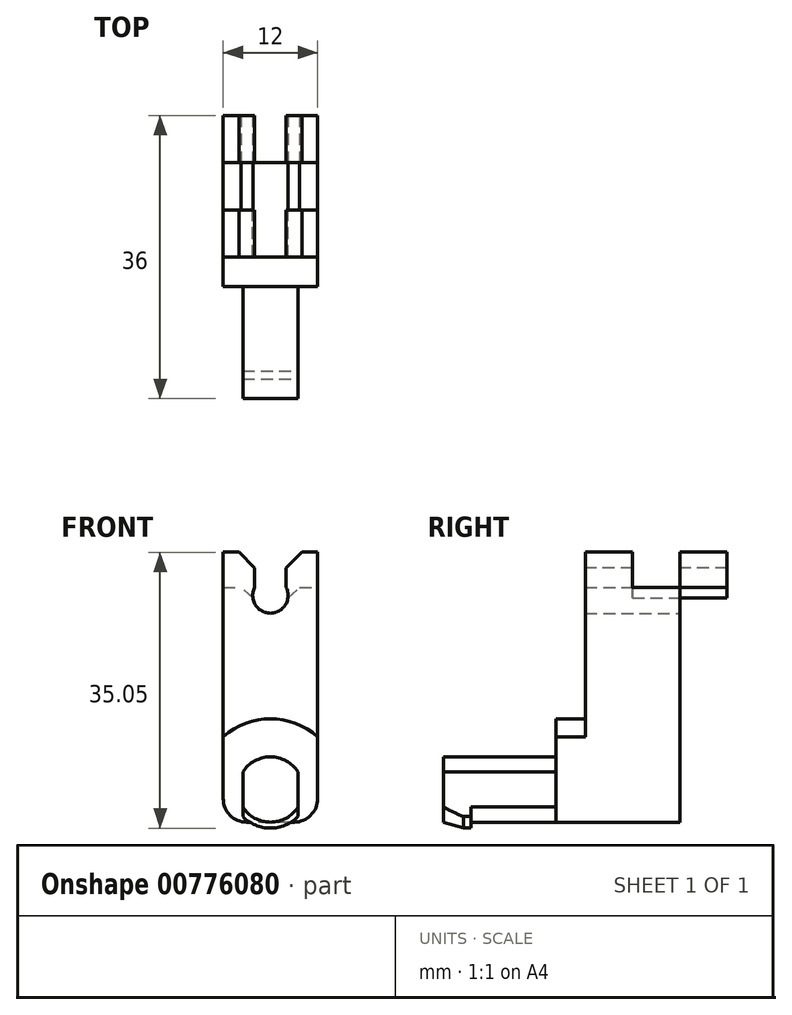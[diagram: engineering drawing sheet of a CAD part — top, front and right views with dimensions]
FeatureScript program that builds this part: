
annotation { "Feature Type Name" : "Feature", "Feature Type Description" : "" }
export const myFeature = defineFeature(function(context is Context, id is Id, definition is map)
    precondition{}
    {
        {
            var Q0;
            Q0=qCreatedBy(makeId("Right.planeOp"),FACE);
            var sketch = newSketch(context, id + "F0", { "sketchPlane" : qUnion([Q0])});
            skLineSegment(sketch, "E0.bottom", {"start": v(-25.14, 2.61) * mm, "end": v(-19.14, 2.61) * mm});
            skLineSegment(sketch, "E0.top", {"start": v(-25.14, -15.39) * mm, "end": v(-19.14, -15.39) * mm});
            skLineSegment(sketch, "E0.left", {"start": v(-25.14, 2.61) * mm, "end": v(-25.14, -15.39) * mm});
            skLineSegment(sketch, "E0.right", {"start": v(-19.14, 2.61) * mm, "end": v(-19.14, -15.39) * mm});
            skSolve(sketch);
        }
        {
            var Q0;
            Q0=makeQuery(id+"F0.imprint","IMPRINT",FACE,{"disambiguationData":[TD([[makeQuery(id+"F0.imprint","IMPRINT",EDGE,{"derivedFrom":sQuery(id+"F0.wireOp",EDGE,"E0.bottom")}),-1.0]])]});
            extrude(context, id + "F1", {"entities" : qUnion([Q0]), "depth" : 8 * mm, "offsetDistance" : 25 * mm});
        }
        {
            var Q0;
            Q0=makeQuery(id+"F1.opExtrude","SWEPT_FACE",FACE,{"disambiguationData":[OSD([sQuery(id+"F0.wireOp",EDGE,"E0.left")])]});
            var sketch = newSketch(context, id + "F2", { "sketchPlane" : qUnion([Q0])});
            skCircle(sketch, "E1", {"center": v(4, -19.54) * mm, "radius": 4.15 * mm});
            skSolve(sketch);
        }
        {
            var Q0;
            Q0=makeQuery(id+"F2.imprint","IMPRINT",FACE,{"disambiguationData":[TD([[makeQuery(id+"F2.imprint","IMPRINT",EDGE,{"derivedFrom":sQuery(id+"F2.wireOp",EDGE,"E1")}),1.0]])]});
            extrude(context, id + "F3", {"entities" : qUnion([Q0]), "depth" : 18 * mm, "offsetDistance" : 25 * mm});
        }
        {
            var Q0;
            Q0=makeQuery(id+"F3.opExtrude","CAP_FACE",FACE,{"disambiguationData":[OSD([sQuery(id+"F2.wireOp",EDGE,"E1")])],"isStart":true});
            var Q1;
            Q1=makeQuery(id+"F1.opExtrude","SWEPT_FACE",FACE,{"disambiguationData":[OSD([sQuery(id+"F0.wireOp",EDGE,"E0.right")])]});
            extrude(context, id + "F4", {"entities" : qUnion([Q0]), "endBound" : BoundingType.UP_TO_SURFACE, "depth" : 25 * mm, "endBoundEntityFace" : qUnion([Q1]), "offsetDistance" : 25 * mm});
        }
        {
            var Q0;
            Q0=makeQuery(id+"F1.opExtrude","SWEPT_FACE",FACE,{"disambiguationData":[OSD([sQuery(id+"F0.wireOp",EDGE,"E0.top")])]});
            var Q1;
            Q1=makeQuery(id+"F4.opExtrude","SWEPT_FACE",FACE,{"disambiguationData":[OSD([sQuery(id+"F2.wireOp",EDGE,"E1")])]});
            extrude(context, id + "F5", {"entities" : qUnion([Q0]), "depth" : (8.4 / 2) * mm, "endBoundEntityFace" : qUnion([Q1]), "offsetDistance" : 25 * mm});
        }
        {
            var Q0;
            Q0=makeQuery(id+"F3.opExtrude","SWEPT_BODY",BODY,{"disambiguationData":[OSD([sQuery(id+"F2.wireOp",EDGE,"E1")])]});
            var Q1;
            Q1=makeQuery(id+"F4.opExtrude","SWEPT_BODY",BODY,{"disambiguationData":[OSD([sQuery(id+"F2.wireOp",EDGE,"E1")])]});
            var Q2;
            Q2=makeQuery(id+"F5.opExtrude","SWEPT_BODY",BODY,{"disambiguationData":[OSD([sQuery(id+"F0.wireOp",EDGE,"E0.top")])]});
            var Q3;
            Q3=makeQuery(id+"F1.opExtrude","SWEPT_BODY",BODY,{"disambiguationData":[OSD([sQuery(id+"F0.wireOp",EDGE,"E0.bottom"),sQuery(id+"F0.wireOp",EDGE,"E0.top"),sQuery(id+"F0.wireOp",EDGE,"E0.left"),sQuery(id+"F0.wireOp",EDGE,"E0.right")])]});
            booleanBodies(context, id + "F6", {"operationType" : BooleanOperationType.UNION, "tools" : qUnion([Q0, Q1, Q2, Q3])});
        }
        {
            var Q0;
            {var subQ0=sQuery(id+"F0.wireOp",EDGE,"E0.top");Q0=makeQuery(id+"F6.opBoolean","MERGE",FACE,{"derivedFrom":[makeQuery(id+"F1.opExtrude","CAP_FACE",FACE,{"disambiguationData":[OSD([sQuery(id+"F0.wireOp",EDGE,"E0.bottom"),subQ0,sQuery(id+"F0.wireOp",EDGE,"E0.left"),sQuery(id+"F0.wireOp",EDGE,"E0.right")])],"isStart":false}),makeQuery(id+"F5.opExtrude","SWEPT_FACE",FACE,{"disambiguationData":[OSD([subQ0]),TDD([makeQuery(id+"F1.opExtrude","CAP_EDGE",EDGE,{"disambiguationData":[OSD([subQ0])],"isStart":false})])]})]});}
            var Q1;
            {var subQ0=sQuery(id+"F0.wireOp",EDGE,"E0.top");Q1=makeQuery(id+"F6.opBoolean","MERGE",FACE,{"derivedFrom":[makeQuery(id+"F1.opExtrude","CAP_FACE",FACE,{"disambiguationData":[OSD([sQuery(id+"F0.wireOp",EDGE,"E0.bottom"),subQ0,sQuery(id+"F0.wireOp",EDGE,"E0.left"),sQuery(id+"F0.wireOp",EDGE,"E0.right")])],"isStart":true}),makeQuery(id+"F5.opExtrude","SWEPT_FACE",FACE,{"disambiguationData":[OSD([subQ0]),TDD([makeQuery(id+"F1.opExtrude","CAP_EDGE",EDGE,{"disambiguationData":[OSD([subQ0])],"isStart":true})])]})]});}
            cPlane(context, id + "F7", {"entities" : qUnion([Q0, Q1]), "cplaneType" : CPlaneType.MID_PLANE, "offset" : 25 * mm, "width" : 150 * mm, "height" : 150 * mm});
        }
        {
            var Q0;
            Q0=qCreatedBy(id+"F7.planeOp",FACE);
            var sketch = newSketch(context, id + "F8", { "sketchPlane" : qUnion([Q0])});
            skLineSegment(sketch, "E2", {"start": v(-39.64, -15.39) * mm, "end": v(-39.64, -14.64) * mm});
            skLineSegment(sketch, "E3", {"start": v(-39.64, -14.64) * mm, "end": v(-40.64, -14.64) * mm});
            skLineSegment(sketch, "E4", {"start": v(-40.64, -14.64) * mm, "end": v(-43.14, -15.39) * mm});
            skLineSegment(sketch, "E5", {"start": v(-43.14, -15.39) * mm, "end": v(-39.64, -15.39) * mm});
            skSolve(sketch);
        }
        {
            var Q0;
            Q0=makeQuery(id+"F8.imprint","IMPRINT",FACE,{"disambiguationData":[TD([[makeQuery(id+"F8.imprint","IMPRINT",EDGE,{"derivedFrom":sQuery(id+"F8.wireOp",EDGE,"E2")}),1.0]])]});
            var Q1;
            {var subQ0=sQuery(id+"F2.wireOp",EDGE,"E1");Q1=makeQuery(id+"F6.opBoolean","MERGE",FACE,{"derivedFrom":[makeQuery(id+"F3.opExtrude","SWEPT_FACE",FACE,{"disambiguationData":[OSD([subQ0])]}),makeQuery(id+"F4.opExtrude","SWEPT_FACE",FACE,{"disambiguationData":[OSD([subQ0])]})]});}
            revolve(context, id + "F9", {"operationType" : NewBodyOperationType.ADD, "surfaceOperationType" : NewSurfaceOperationType.NEW, "entities" : qUnion([Q0]), "axis" : qUnion([Q1]), "revolveType" : RevolveType.SYMMETRIC, "angle" : 360 * degree});
        }
        {
            var Q0;
            Q0=makeQuery(id+"F1.opExtrude","SWEPT_FACE",FACE,{"disambiguationData":[OSD([sQuery(id+"F0.wireOp",EDGE,"E0.bottom")])]});
            extrude(context, id + "F10", {"entities" : qUnion([Q0]), "depth" : 6 * mm, "offsetDistance" : 25 * mm});
        }
        {
            var Q0;
            Q0=makeQuery(id+"F10.opExtrude","SWEPT_FACE",FACE,{"disambiguationData":[OSD([sQuery(id+"F0.wireOp",EDGE,"E0.bottom"),sQuery(id+"F0.wireOp",EDGE,"E0.right")])]});
            var sketch = newSketch(context, id + "F11", { "sketchPlane" : qUnion([Q0])});
            skCircle(sketch, "E6", {"center": v(-4, 5.11) * mm, "radius": 2.25 * mm});
            skSolve(sketch);
        }
        {
            var Q0;
            Q0=makeQuery(id+"F10.opExtrude","SWEPT_BODY",BODY,{"disambiguationData":[OSD([sQuery(id+"F0.wireOp",EDGE,"E0.bottom")])]});
            var Q1;
            Q1=makeQuery(id+"F3.opExtrude","SWEPT_BODY",BODY,{"disambiguationData":[OSD([sQuery(id+"F2.wireOp",EDGE,"E1")])]});
            booleanBodies(context, id + "F12", {"operationType" : BooleanOperationType.UNION, "tools" : qUnion([Q0, Q1])});
        }
        {
            var Q0;
            Q0=makeQuery(id+"F11.imprint","IMPRINT",FACE,{"disambiguationData":[TD([[makeQuery(id+"F11.imprint","IMPRINT",EDGE,{"derivedFrom":sQuery(id+"F11.wireOp",EDGE,"E6")}),1.0]])]});
            extrude(context, id + "F13", {"entities" : qUnion([Q0]), "operationType" : NewBodyOperationType.REMOVE, "oppositeDirection" : true, "depth" : 25 * mm, "offsetDistance" : 25 * mm});
        }
        {
            var Q0;
            {var subQ4=sQuery(id+"F11.wireOp",EDGE,"E6");Q0=makeQuery(id+"F11.imprint","IMPRINT",FACE,{"disambiguationData":[TD([[makeQuery(id+"F11.imprint","IMPRINT",EDGE,{"derivedFrom":subQ4}),-1.0]])]});}
            var sketch = newSketch(context, id + "F14", { "sketchPlane" : qUnion([Q0])});
            skLineSegment(sketch, "E7.bottom", {"start": v(-6, 9.61) * mm, "end": v(-2, 9.61) * mm});
            skLineSegment(sketch, "E7.top", {"start": v(-6, 5.11) * mm, "end": v(-2, 5.11) * mm});
            skLineSegment(sketch, "E7.left", {"start": v(-6, 9.61) * mm, "end": v(-6, 5.11) * mm});
            skLineSegment(sketch, "E7.right", {"start": v(-2, 9.61) * mm, "end": v(-2, 5.11) * mm});
            skSolve(sketch);
        }
        {
            var Q0;
            Q0 = qSketchRegion(id + "F14", true);
            extrude(context, id + "F15", {"entities" : qUnion([Q0]), "operationType" : NewBodyOperationType.REMOVE, "oppositeDirection" : true, "depth" : 25 * mm, "offsetDistance" : 25 * mm});
        }
        {
            var Q0;
            {var subQ0=sQuery(id+"F0.wireOp",EDGE,"E0.left");Q0=makeQuery(id+"F12.opBoolean","MERGE",FACE,{"derivedFrom":[makeQuery(id+"F6.opBoolean","MERGE",FACE,{"derivedFrom":[makeQuery(id+"F1.opExtrude","SWEPT_FACE",FACE,{"disambiguationData":[OSD([subQ0])]}),makeQuery(id+"F4.opExtrude","CAP_FACE",FACE,{"disambiguationData":[OSD([sQuery(id+"F2.wireOp",EDGE,"E1")])],"isStart":true}),makeQuery(id+"F5.opExtrude","SWEPT_FACE",FACE,{"disambiguationData":[OSD([sQuery(id+"F0.wireOp",EDGE,"E0.top"),subQ0])]})]}),makeQuery(id+"F10.opExtrude","SWEPT_FACE",FACE,{"disambiguationData":[OSD([sQuery(id+"F0.wireOp",EDGE,"E0.bottom"),subQ0])]})]});}
            var sketch = newSketch(context, id + "F16", { "sketchPlane" : qUnion([Q0])});
            skLineSegment(sketch, "E8.bottom", {"start": v(-2, -9.26) * mm, "end": v(0.5, -9.26) * mm});
            skLineSegment(sketch, "E8.top", {"start": v(-2, -26.84) * mm, "end": v(0.5, -26.84) * mm});
            skLineSegment(sketch, "E8.left", {"start": v(-2, -9.26) * mm, "end": v(-2, -26.84) * mm});
            skLineSegment(sketch, "E8.right", {"start": v(0.5, -9.26) * mm, "end": v(0.5, -26.84) * mm});
            skLineSegment(sketch, "E9.bottom", {"start": v(11, -9.26) * mm, "end": v(7.5, -9.26) * mm});
            skLineSegment(sketch, "E9.top", {"start": v(11, -26.84) * mm, "end": v(7.5, -26.84) * mm});
            skLineSegment(sketch, "E9.left", {"start": v(11, -9.26) * mm, "end": v(11, -26.84) * mm});
            skLineSegment(sketch, "E9.right", {"start": v(7.5, -9.26) * mm, "end": v(7.5, -26.84) * mm});
            skSolve(sketch);
        }
        {
            var Q0;
            Q0 = qSketchRegion(id + "F16", true);
            extrude(context, id + "F17", {"entities" : qUnion([Q0]), "operationType" : NewBodyOperationType.REMOVE, "endBound" : BoundingType.THROUGH_ALL, "depth" : 25 * mm, "offsetDistance" : 25 * mm});
        }
        {
            var Q0;
            {var subQ1=sQuery(id+"F0.wireOp",EDGE,"E0.bottom");Q0=makeQuery(id+"F15.boolean.opBoolean","SPLIT",FACE,{"disambiguationData":[TD([makeQuery(id+"F15.opExtrude","SWEPT_FACE",FACE,{"disambiguationData":[OSD([sQuery(id+"F14.wireOp",EDGE,"E7.right")])]})])],"derivedFrom":makeQuery(id+"F10.opExtrude","CAP_FACE",FACE,{"disambiguationData":[OSD([subQ1])],"isStart":false})});}
            var sketch = newSketch(context, id + "F18", { "sketchPlane" : qUnion([Q0])});
            skLineSegment(sketch, "E10.bottom", {"start": v(-2, -19.14) * mm, "end": v(0, -19.14) * mm});
            skLineSegment(sketch, "E10.top", {"start": v(-2, -25.14) * mm, "end": v(0, -25.14) * mm});
            skLineSegment(sketch, "E10.left", {"start": v(-2, -19.14) * mm, "end": v(-2, -25.14) * mm});
            skLineSegment(sketch, "E10.right", {"start": v(0, -19.14) * mm, "end": v(0, -25.14) * mm});
            skPoint(sketch, "E11.oppositeSnap0", {"position": v(0, -22.14) * mm});
            skLineSegment(sketch, "E11.bottom", {"start": v(8, -19.14) * mm, "end": v(10, -19.14) * mm});
            skLineSegment(sketch, "E11.top", {"start": v(8, -25.14) * mm, "end": v(10, -25.14) * mm});
            skLineSegment(sketch, "E11.left", {"start": v(8, -19.14) * mm, "end": v(8, -25.14) * mm});
            skLineSegment(sketch, "E11.right", {"start": v(10, -19.14) * mm, "end": v(10, -25.14) * mm});
            skSolve(sketch);
        }
        {
            var Q0;
            Q0=makeQuery(id+"F18.imprint","IMPRINT",FACE,{"disambiguationData":[TD([[makeQuery(id+"F18.imprint","IMPRINT",EDGE,{"derivedFrom":sQuery(id+"F18.wireOp",EDGE,"E10.bottom")}),-1.0]])]});
            var Q1;
            Q1=makeQuery(id+"F18.imprint","IMPRINT",FACE,{"disambiguationData":[TD([[makeQuery(id+"F18.imprint","IMPRINT",EDGE,{"derivedFrom":sQuery(id+"F18.wireOp",EDGE,"E11.bottom")}),-1.0]])]});
            extrude(context, id + "F19", {"entities" : qUnion([Q0, Q1]), "operationType" : NewBodyOperationType.ADD, "oppositeDirection" : true, "depth" : 30 * mm, "offsetDistance" : 25 * mm});
        }
        {
            var Q0;
            {var subQ0=sQuery(id+"F0.wireOp",EDGE,"E0.right");Q0=makeQuery(id+"F19.boolean.opBoolean","MERGE",FACE,{"derivedFrom":[makeQuery(id+"F12.opBoolean","MERGE",FACE,{"derivedFrom":[makeQuery(id+"F6.opBoolean","MERGE",FACE,{"derivedFrom":[makeQuery(id+"F1.opExtrude","SWEPT_FACE",FACE,{"disambiguationData":[OSD([subQ0])]}),makeQuery(id+"F4.opExtrude","CAP_FACE",FACE,{"disambiguationData":[OSD([sQuery(id+"F2.wireOp",EDGE,"E1")])],"isStart":false}),makeQuery(id+"F5.opExtrude","SWEPT_FACE",FACE,{"disambiguationData":[OSD([sQuery(id+"F0.wireOp",EDGE,"E0.top"),subQ0])]})]}),makeQuery(id+"F10.opExtrude","SWEPT_FACE",FACE,{"disambiguationData":[OSD([sQuery(id+"F0.wireOp",EDGE,"E0.bottom"),subQ0])]})]}),makeQuery(id+"F19.opExtrude","SWEPT_FACE",FACE,{"disambiguationData":[OSD([sQuery(id+"F18.wireOp",EDGE,"E10.bottom")])]}),makeQuery(id+"F19.opExtrude","SWEPT_FACE",FACE,{"disambiguationData":[OSD([sQuery(id+"F18.wireOp",EDGE,"E11.bottom")])]})]});}
            var sketch = newSketch(context, id + "F20", { "sketchPlane" : qUnion([Q0])});
            skLineSegment(sketch, "E12.bottom", {"start": v(-10, -13.69) * mm, "end": v(2, -13.69) * mm});
            skLineSegment(sketch, "E12.top", {"start": v(-10, -23.69) * mm, "end": v(2, -23.69) * mm});
            skLineSegment(sketch, "E12.left", {"start": v(-10, -13.69) * mm, "end": v(-10, -23.69) * mm});
            skLineSegment(sketch, "E12.right", {"start": v(2, -13.69) * mm, "end": v(2, -23.69) * mm});
            skSolve(sketch);
        }
        {
            var Q0;
            {var subQ0=sQuery(id+"F18.wireOp",EDGE,"E11.bottom");var subQ2=makeQuery(id+"F19.opExtrude","CAP_EDGE",EDGE,{"disambiguationData":[OSD([subQ0])],"isStart":false});Q0=makeQuery(id+"F20.imprint","IMPRINT",FACE,{"disambiguationData":[TD([[makeQuery(id+"F20.imprint","IMPRINT",EDGE,{"derivedFrom":subQ2}),1.0]])]});}
            var Q1;
            {var subQ0=sQuery(id+"F18.wireOp",EDGE,"E10.bottom");var subQ4=makeQuery(id+"F19.opExtrude","CAP_EDGE",EDGE,{"disambiguationData":[OSD([subQ0])],"isStart":false});Q1=makeQuery(id+"F20.imprint","IMPRINT",FACE,{"disambiguationData":[TD([[makeQuery(id+"F20.imprint","IMPRINT",EDGE,{"derivedFrom":subQ4}),1.0]])]});}
            var Q2;
            {var subQ5=sQuery(id+"F20.wireOp",EDGE,"E12.bottom");Q2=makeQuery(id+"F20.imprint","IMPRINT",FACE,{"disambiguationData":[TD([[makeQuery(id+"F20.imprint","IMPRINT",EDGE,{"derivedFrom":subQ5}),-1.0]])]});}
            var Q3;
            {var subQ0=sQuery(id+"F0.wireOp",EDGE,"E0.left");Q3=makeQuery(id+"F19.boolean.opBoolean","MERGE",FACE,{"derivedFrom":[makeQuery(id+"F17.boolean.opBoolean","MERGE",FACE,{"derivedFrom":[makeQuery(id+"F12.opBoolean","MERGE",FACE,{"derivedFrom":[makeQuery(id+"F6.opBoolean","MERGE",FACE,{"derivedFrom":[makeQuery(id+"F1.opExtrude","SWEPT_FACE",FACE,{"disambiguationData":[OSD([subQ0])]}),makeQuery(id+"F4.opExtrude","CAP_FACE",FACE,{"disambiguationData":[OSD([sQuery(id+"F2.wireOp",EDGE,"E1")])],"isStart":true}),makeQuery(id+"F5.opExtrude","SWEPT_FACE",FACE,{"disambiguationData":[OSD([sQuery(id+"F0.wireOp",EDGE,"E0.top"),subQ0])]})]}),makeQuery(id+"F10.opExtrude","SWEPT_FACE",FACE,{"disambiguationData":[OSD([sQuery(id+"F0.wireOp",EDGE,"E0.bottom"),subQ0])]})]})],"fromTools":[makeQuery(id+"F17.opExtrude","CAP_FACE",FACE,{"disambiguationData":[OSD([sQuery(id+"F16.wireOp",EDGE,"E8.bottom"),sQuery(id+"F16.wireOp",EDGE,"E8.top"),sQuery(id+"F16.wireOp",EDGE,"E8.left"),sQuery(id+"F16.wireOp",EDGE,"E8.right")])],"isStart":true}),makeQuery(id+"F17.opExtrude","CAP_FACE",FACE,{"disambiguationData":[OSD([sQuery(id+"F16.wireOp",EDGE,"E9.bottom"),sQuery(id+"F16.wireOp",EDGE,"E9.top"),sQuery(id+"F16.wireOp",EDGE,"E9.left"),sQuery(id+"F16.wireOp",EDGE,"E9.right")])],"isStart":true})]}),makeQuery(id+"F19.opExtrude","SWEPT_FACE",FACE,{"disambiguationData":[OSD([sQuery(id+"F18.wireOp",EDGE,"E10.top")])]}),makeQuery(id+"F19.opExtrude","SWEPT_FACE",FACE,{"disambiguationData":[OSD([sQuery(id+"F18.wireOp",EDGE,"E11.top")])]})]});}
            extrude(context, id + "F21", {"entities" : qUnion([Q0, Q1, Q2]), "operationType" : NewBodyOperationType.ADD, "endBound" : BoundingType.UP_TO_SURFACE, "oppositeDirection" : true, "depth" : 25 * mm, "endBoundEntityFace" : qUnion([Q3]), "offsetDistance" : 25 * mm});
        }
        {
            var Q0;
            {var subQ0=sQuery(id+"F0.wireOp",EDGE,"E0.left");Q0=makeQuery(id+"F21.boolean.opBoolean","MERGE",FACE,{"derivedFrom":[makeQuery(id+"F19.boolean.opBoolean","MERGE",FACE,{"derivedFrom":[makeQuery(id+"F17.boolean.opBoolean","MERGE",FACE,{"derivedFrom":[makeQuery(id+"F12.opBoolean","MERGE",FACE,{"derivedFrom":[makeQuery(id+"F6.opBoolean","MERGE",FACE,{"derivedFrom":[makeQuery(id+"F1.opExtrude","SWEPT_FACE",FACE,{"disambiguationData":[OSD([subQ0])]}),makeQuery(id+"F4.opExtrude","CAP_FACE",FACE,{"disambiguationData":[OSD([sQuery(id+"F2.wireOp",EDGE,"E1")])],"isStart":true}),makeQuery(id+"F5.opExtrude","SWEPT_FACE",FACE,{"disambiguationData":[OSD([sQuery(id+"F0.wireOp",EDGE,"E0.top"),subQ0])]})]}),makeQuery(id+"F10.opExtrude","SWEPT_FACE",FACE,{"disambiguationData":[OSD([sQuery(id+"F0.wireOp",EDGE,"E0.bottom"),subQ0])]})]})],"fromTools":[makeQuery(id+"F17.opExtrude","CAP_FACE",FACE,{"disambiguationData":[OSD([sQuery(id+"F16.wireOp",EDGE,"E8.bottom"),sQuery(id+"F16.wireOp",EDGE,"E8.top"),sQuery(id+"F16.wireOp",EDGE,"E8.left"),sQuery(id+"F16.wireOp",EDGE,"E8.right")])],"isStart":true}),makeQuery(id+"F17.opExtrude","CAP_FACE",FACE,{"disambiguationData":[OSD([sQuery(id+"F16.wireOp",EDGE,"E9.bottom"),sQuery(id+"F16.wireOp",EDGE,"E9.top"),sQuery(id+"F16.wireOp",EDGE,"E9.left"),sQuery(id+"F16.wireOp",EDGE,"E9.right")])],"isStart":true})]}),makeQuery(id+"F19.opExtrude","SWEPT_FACE",FACE,{"disambiguationData":[OSD([sQuery(id+"F18.wireOp",EDGE,"E10.top")])]}),makeQuery(id+"F19.opExtrude","SWEPT_FACE",FACE,{"disambiguationData":[OSD([sQuery(id+"F18.wireOp",EDGE,"E11.top")])]})]}),makeQuery(id+"F21.opExtrude","CAP_FACE",FACE,{"disambiguationData":[OSD([sQuery(id+"F20.wireOp",EDGE,"E12.bottom"),sQuery(id+"F20.wireOp",EDGE,"E12.top"),sQuery(id+"F20.wireOp",EDGE,"E12.left"),sQuery(id+"F20.wireOp",EDGE,"E12.right")])],"isStart":false})]});}
            var sketch = newSketch(context, id + "F22", { "sketchPlane" : qUnion([Q0])});
            skArc(sketch, "E13", {"start": v(10, -12.83) * mm, "mid": v(4, -10.54) * mm, "end": v(-2, -12.83) * mm});
            skLineSegment(sketch, "E14.0", {"start": v(10, -23.69) * mm, "end": v(10, -12.83) * mm});
            skLineSegment(sketch, "E15.0", {"start": v(-2, -23.69) * mm, "end": v(-2, -12.83) * mm});
            skPoint(sketch, "E16.orphan", {"position": v(10, 8.61) * mm});
            skPoint(sketch, "E17.orphan", {"position": v(-2, 8.61) * mm});
            skLineSegment(sketch, "E18", {"start": v(-2, -23.69) * mm, "end": v(10, -23.69) * mm});
            skSolve(sketch);
        }
        {
            var Q0;
            Q0 = qSketchRegion(id + "F22", true);
            extrude(context, id + "F23", {"entities" : qUnion([Q0]), "operationType" : NewBodyOperationType.ADD, "depth" : 3.75 * mm, "offsetDistance" : 25 * mm});
        }
        {
            var Q0;
            Q0=makeQuery(id+"F23.boolean.opBoolean","MERGE",EDGE,{"derivedFrom":[makeQuery(id+"F21.opExtrude","SWEPT_EDGE",EDGE,{"disambiguationData":[OSD([sQuery(id+"F20.wireOp",EDGE,"E12.top"),sQuery(id+"F20.wireOp",EDGE,"E12.right")])]}),makeQuery(id+"F23.opExtrude","SWEPT_EDGE",EDGE,{"disambiguationData":[OSD([sQuery(id+"F22.wireOp",EDGE,"E15.0"),sQuery(id+"F22.wireOp",EDGE,"E18")])]})]});
            var Q1;
            Q1=makeQuery(id+"F23.boolean.opBoolean","MERGE",EDGE,{"derivedFrom":[makeQuery(id+"F21.opExtrude","SWEPT_EDGE",EDGE,{"disambiguationData":[OSD([sQuery(id+"F20.wireOp",EDGE,"E12.top"),sQuery(id+"F20.wireOp",EDGE,"E12.left")])]}),makeQuery(id+"F23.opExtrude","SWEPT_EDGE",EDGE,{"disambiguationData":[OSD([sQuery(id+"F22.wireOp",EDGE,"E14.0"),sQuery(id+"F22.wireOp",EDGE,"E18")])]})]});
            fillet(context, id + "F24", {"entities" : qUnion([Q0, Q1]), "radius" : 3 * mm, "tangentPropagation" : true, "allowEdgeOverflow" : false});
        }
        {
            var Q0;
            Q0=makeQuery(id+"F23.opExtrude","CAP_FACE",FACE,{"disambiguationData":[OSD([sQuery(id+"F22.wireOp",EDGE,"E13"),sQuery(id+"F22.wireOp",EDGE,"E14.0"),sQuery(id+"F22.wireOp",EDGE,"E15.0"),sQuery(id+"F22.wireOp",EDGE,"E18")])],"isStart":false});
            var sketch = newSketch(context, id + "F25", { "sketchPlane" : qUnion([Q0])});
            skArc(sketch, "E19", {"start": v(8.15, -19.54) * mm, "mid": v(4, -15.39) * mm, "end": v(-0.15, -19.54) * mm});
            skPoint(sketch, "E19.perimeterSnap0", {"position": v(10, -16.76) * mm});
            skLineSegment(sketch, "E20", {"start": v(8.15, -19.54) * mm, "end": v(10, -19.54) * mm});
            skLineSegment(sketch, "E21", {"start": v(10, -19.54) * mm, "end": v(10, -10.54) * mm});
            skLineSegment(sketch, "E22", {"start": v(10, -10.54) * mm, "end": v(-2, -10.54) * mm});
            skLineSegment(sketch, "E23", {"start": v(-2, -10.54) * mm, "end": v(-2, -19.54) * mm});
            skLineSegment(sketch, "E24", {"start": v(-2, -19.54) * mm, "end": v(-0.15, -19.54) * mm});
            skSolve(sketch);
        }
        {
            var Q0;
            Q0 = qSketchRegion(id + "F25", true);
            extrude(context, id + "F26", {"entities" : qUnion([Q0]), "operationType" : NewBodyOperationType.REMOVE, "depth" : 25 * mm, "offsetDistance" : 25 * mm});
        }
        {
            var Q0;
            {var subQ1=sQuery(id+"F0.wireOp",EDGE,"E0.bottom");Q0=makeQuery(id+"F19.boolean.opBoolean","MERGE",FACE,{"derivedFrom":[makeQuery(id+"F15.boolean.opBoolean","SPLIT",FACE,{"disambiguationData":[TD([makeQuery(id+"F15.opExtrude","SWEPT_FACE",FACE,{"disambiguationData":[OSD([sQuery(id+"F14.wireOp",EDGE,"E7.right")])]})])],"derivedFrom":makeQuery(id+"F10.opExtrude","CAP_FACE",FACE,{"disambiguationData":[OSD([subQ1])],"isStart":false})}),makeQuery(id+"F19.opExtrude","CAP_FACE",FACE,{"disambiguationData":[OSD([sQuery(id+"F18.wireOp",EDGE,"E10.bottom"),sQuery(id+"F18.wireOp",EDGE,"E10.top"),sQuery(id+"F18.wireOp",EDGE,"E10.left"),sQuery(id+"F18.wireOp",EDGE,"E10.right")])],"isStart":true})]});}
            var Q1;
            {var subQ1=sQuery(id+"F0.wireOp",EDGE,"E0.bottom");Q1=makeQuery(id+"F19.boolean.opBoolean","MERGE",FACE,{"derivedFrom":[makeQuery(id+"F15.boolean.opBoolean","SPLIT",FACE,{"disambiguationData":[TD([makeQuery(id+"F15.opExtrude","SWEPT_FACE",FACE,{"disambiguationData":[OSD([sQuery(id+"F14.wireOp",EDGE,"E7.left")])]})])],"derivedFrom":makeQuery(id+"F10.opExtrude","CAP_FACE",FACE,{"disambiguationData":[OSD([subQ1])],"isStart":false})}),makeQuery(id+"F19.opExtrude","CAP_FACE",FACE,{"disambiguationData":[OSD([sQuery(id+"F18.wireOp",EDGE,"E11.bottom"),sQuery(id+"F18.wireOp",EDGE,"E11.top"),sQuery(id+"F18.wireOp",EDGE,"E11.left"),sQuery(id+"F18.wireOp",EDGE,"E11.right")])],"isStart":true})]});}
            extrude(context, id + "F27", {"entities" : qUnion([Q0, Q1]), "operationType" : NewBodyOperationType.ADD, "depth" : 2 * mm, "offsetDistance" : 25 * mm});
        }
        {
            var Q0;
            Q0=makeQuery(id+"F27.opExtrude","CAP_EDGE",EDGE,{"disambiguationData":[OSD([sQuery(id+"F0.wireOp",EDGE,"E0.bottom"),sQuery(id+"F14.wireOp",EDGE,"E7.right")])],"isStart":false});
            var Q1;
            Q1=makeQuery(id+"F27.opExtrude","CAP_EDGE",EDGE,{"disambiguationData":[OSD([sQuery(id+"F0.wireOp",EDGE,"E0.bottom"),sQuery(id+"F14.wireOp",EDGE,"E7.left")])],"isStart":false});
            chamfer(context, id + "F28", {"entities" : qUnion([Q0, Q1]), "width" : 2 * mm, "tangentPropagation" : true});
        }
        {
            var Q0;
            {var subQ0=sQuery(id+"F18.wireOp",EDGE,"E11.bottom");var subQ1=sQuery(id+"F0.wireOp",EDGE,"E0.right");var subQ2=sQuery(id+"F0.wireOp",EDGE,"E0.bottom");var subQ3=sQuery(id+"F18.wireOp",EDGE,"E10.bottom");Q0=makeQuery(id+"F27.boolean.opBoolean","MERGE",FACE,{"derivedFrom":[makeQuery(id+"F21.boolean.opBoolean","MERGE",FACE,{"derivedFrom":[makeQuery(id+"F19.boolean.opBoolean","MERGE",FACE,{"derivedFrom":[makeQuery(id+"F12.opBoolean","MERGE",FACE,{"derivedFrom":[makeQuery(id+"F6.opBoolean","MERGE",FACE,{"derivedFrom":[makeQuery(id+"F1.opExtrude","SWEPT_FACE",FACE,{"disambiguationData":[OSD([subQ1])]}),makeQuery(id+"F4.opExtrude","CAP_FACE",FACE,{"disambiguationData":[OSD([sQuery(id+"F2.wireOp",EDGE,"E1")])],"isStart":false}),makeQuery(id+"F5.opExtrude","SWEPT_FACE",FACE,{"disambiguationData":[OSD([sQuery(id+"F0.wireOp",EDGE,"E0.top"),subQ1])]})]}),makeQuery(id+"F10.opExtrude","SWEPT_FACE",FACE,{"disambiguationData":[OSD([subQ2,subQ1])]})]}),makeQuery(id+"F19.opExtrude","SWEPT_FACE",FACE,{"disambiguationData":[OSD([subQ3])]}),makeQuery(id+"F19.opExtrude","SWEPT_FACE",FACE,{"disambiguationData":[OSD([subQ0])]})]}),makeQuery(id+"F21.opExtrude","CAP_FACE",FACE,{"disambiguationData":[OSD([sQuery(id+"F20.wireOp",EDGE,"E12.bottom"),sQuery(id+"F20.wireOp",EDGE,"E12.top"),sQuery(id+"F20.wireOp",EDGE,"E12.left"),sQuery(id+"F20.wireOp",EDGE,"E12.right")])],"isStart":true})]}),makeQuery(id+"F27.opExtrude","SWEPT_FACE",FACE,{"disambiguationData":[OSD([subQ2,subQ1,subQ3])]}),makeQuery(id+"F27.opExtrude","SWEPT_FACE",FACE,{"disambiguationData":[OSD([subQ2,subQ1,subQ0])]})]});}
            var sketch = newSketch(context, id + "F29", { "sketchPlane" : qUnion([Q0])});
            skLineSegment(sketch, "E25.0.3", {"start": v(-10, 6.11) * mm, "end": v(-10, -20.69) * mm});
            skArc(sketch, "E25.0.4", {"start": v(-10, -20.69) * mm, "mid": v(-9.12, -22.8) * mm, "end": v(-7, -23.69) * mm});
            skLineSegment(sketch, "E25.0.5", {"start": v(-7, -23.69) * mm, "end": v(-1, -23.69) * mm});
            skArc(sketch, "E25.0.6", {"start": v(-1, -23.69) * mm, "mid": v(1.12, -22.8) * mm, "end": v(2, -20.69) * mm});
            skLineSegment(sketch, "E25.0.7", {"start": v(2, -20.69) * mm, "end": v(2, 6.11) * mm});
            skArc(sketch, "E25.0.11", {"start": v(-1.98, 6.11) * mm, "mid": v(-4, 2.86) * mm, "end": v(-6.02, 6.11) * mm});
            skLineSegment(sketch, "E26", {"start": v(2, 6.11) * mm, "end": v(-10, 6.11) * mm});
            skPoint(sketch, "E27.orphan", {"position": v(-10, 10.61) * mm});
            skPoint(sketch, "E28.orphan", {"position": v(2, 10.61) * mm});
            skPoint(sketch, "E29.orphan", {"position": v(-2, 6.14) * mm});
            skPoint(sketch, "E30.orphan", {"position": v(-6, 6.14) * mm});
            skSolve(sketch);
        }
        {
            var Q0;
            {var subQ0=sQuery(id+"F29.wireOp",EDGE,"E25.0.3");Q0=makeQuery(id+"F29.imprint","IMPRINT",FACE,{"disambiguationData":[TD([[makeQuery(id+"F29.imprint","IMPRINT",EDGE,{"derivedFrom":subQ0}),-1.0]])]});}
            extrude(context, id + "F30", {"entities" : qUnion([Q0]), "operationType" : NewBodyOperationType.ADD, "depth" : 6 * mm, "offsetDistance" : 25 * mm});
        }
        {
            var Q0;
            Q0=makeQuery(id+"F30.opExtrude","SWEPT_EDGE",EDGE,{"disambiguationData":[OSD([sQuery(id+"F0.wireOp",EDGE,"E0.bottom"),sQuery(id+"F14.wireOp",EDGE,"E7.right"),sQuery(id+"F29.wireOp",EDGE,"E26")])]});
            var Q1;
            Q1=makeQuery(id+"F30.opExtrude","SWEPT_EDGE",EDGE,{"disambiguationData":[OSD([sQuery(id+"F0.wireOp",EDGE,"E0.bottom"),sQuery(id+"F14.wireOp",EDGE,"E7.left"),sQuery(id+"F29.wireOp",EDGE,"E26")])]});
            chamfer(context, id + "F31", {"entities" : qUnion([Q0, Q1]), "width" : 1.5 * mm, "tangentPropagation" : true});
        }
        {
            var Q0;
            Q0=makeQuery(id+"F30.opExtrude","CAP_FACE",FACE,{"disambiguationData":[OSD([sQuery(id+"F29.wireOp",EDGE,"E25.0.3"),sQuery(id+"F29.wireOp",EDGE,"E25.0.4"),sQuery(id+"F29.wireOp",EDGE,"E25.0.5"),sQuery(id+"F29.wireOp",EDGE,"E25.0.6"),sQuery(id+"F29.wireOp",EDGE,"E25.0.7"),sQuery(id+"F29.wireOp",EDGE,"E25.0.11"),sQuery(id+"F29.wireOp",EDGE,"E26")])],"isStart":false});
            var sketch = newSketch(context, id + "F32", { "sketchPlane" : qUnion([Q0])});
            skLineSegment(sketch, "E31.0.0", {"start": v(-10, 10.61) * mm, "end": v(-8, 10.61) * mm});
            skLineSegment(sketch, "E31.0.1", {"start": v(-8, 10.61) * mm, "end": v(-6, 8.61) * mm});
            skLineSegment(sketch, "E31.0.2", {"start": v(-6, 8.61) * mm, "end": v(-6, 6.14) * mm});
            skArc(sketch, "E31.0.3", {"start": v(-6, 6.14) * mm, "mid": v(-4, 2.86) * mm, "end": v(-2, 6.14) * mm});
            skLineSegment(sketch, "E31.0.4", {"start": v(-2, 6.14) * mm, "end": v(-2, 8.61) * mm});
            skLineSegment(sketch, "E31.0.5", {"start": v(-2, 8.61) * mm, "end": v(0, 10.61) * mm});
            skLineSegment(sketch, "E31.0.6", {"start": v(0, 10.61) * mm, "end": v(2, 10.61) * mm});
            skLineSegment(sketch, "E31.0.7", {"start": v(2, 10.61) * mm, "end": v(2, -12.83) * mm});
            skLineSegment(sketch, "E31.0.9", {"start": v(-10, -12.83) * mm, "end": v(-10, 10.61) * mm});
            skArc(sketch, "E32.0.2", {"start": v(-1.75, 5.16) * mm, "mid": v(-4, 2.86) * mm, "end": v(-6.25, 5.16) * mm});
            skLineSegment(sketch, "E32.0.5", {"start": v(-10, 6.11) * mm, "end": v(-10, -20.69) * mm});
            skArc(sketch, "E32.0.6", {"start": v(-10, -20.69) * mm, "mid": v(-9.12, -22.8) * mm, "end": v(-7, -23.69) * mm});
            skLineSegment(sketch, "E32.0.7", {"start": v(-7, -23.69) * mm, "end": v(-1, -23.69) * mm});
            skArc(sketch, "E32.0.8", {"start": v(-1, -23.69) * mm, "mid": v(1.12, -22.8) * mm, "end": v(2, -20.69) * mm});
            skLineSegment(sketch, "E32.0.9", {"start": v(2, -20.69) * mm, "end": v(2, 6.11) * mm});
            skSolve(sketch);
        }
        {
            var Q0;
            {var subQ6=sQuery(id+"F32.wireOp",EDGE,"E31.0.4");Q0=makeQuery(id+"F32.imprint","IMPRINT",FACE,{"disambiguationData":[TD([[makeQuery(id+"F32.imprint","IMPRINT",EDGE,{"derivedFrom":subQ6}),-1.0]])]});}
            var Q1;
            Q1=makeQuery(id+"F32.imprint","IMPRINT",FACE,{"disambiguationData":[TD([[makeQuery(id+"F32.imprint","IMPRINT",EDGE,{"derivedFrom":sQuery(id+"F32.wireOp",EDGE,"E31.0.0")}),-1.0]])]});
            var Q2;
            Q2=makeQuery(id+"F32.imprint","IMPRINT",FACE,{"disambiguationData":[TD([[makeQuery(id+"F32.imprint","IMPRINT",EDGE,{"derivedFrom":sQuery(id+"F32.wireOp",EDGE,"E32.0.2")}),-1.0]])]});
            extrude(context, id + "F33", {"entities" : qUnion([Q0, Q1, Q2]), "operationType" : NewBodyOperationType.ADD, "depth" : 6 * mm, "offsetDistance" : 25 * mm});
        }
    });
